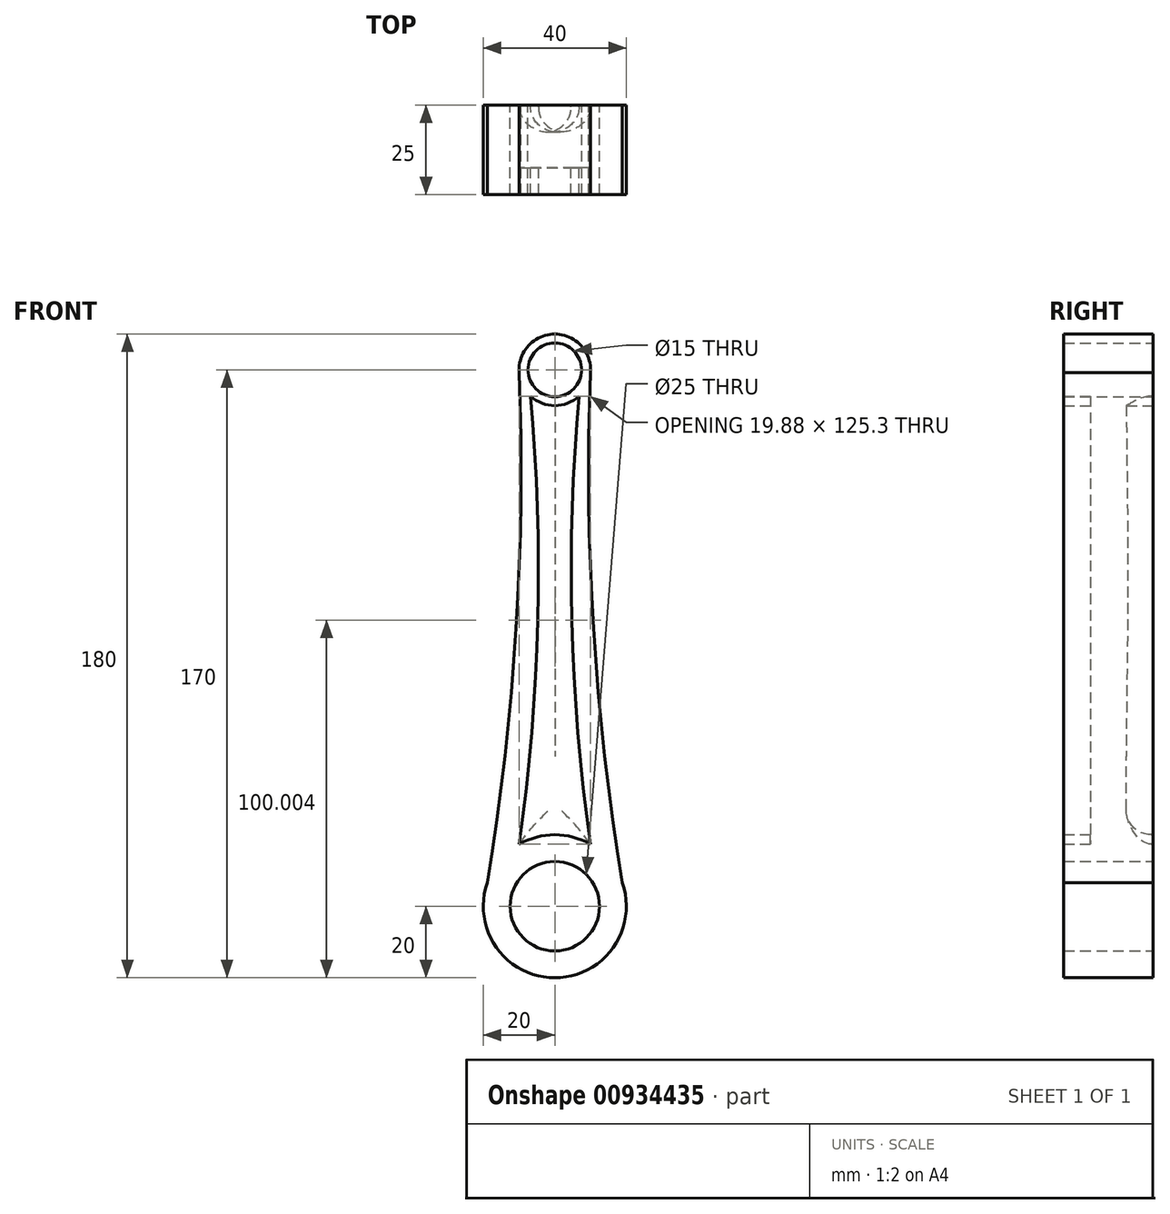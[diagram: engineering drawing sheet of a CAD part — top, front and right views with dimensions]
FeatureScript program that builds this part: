
annotation { "Feature Type Name" : "Feature", "Feature Type Description" : "" }
export const myFeature = defineFeature(function(context is Context, id is Id, definition is map)
    precondition{}
    {
        {
            var Q0;
            Q0=qCreatedBy(makeId("Front.planeOp"),FACE);
            var sketch = newSketch(context, id + "F0", { "sketchPlane" : qUnion([Q0])});
            skArc(sketch, "E0", {"start": v(-18.88, 6.6) * mm, "mid": v(15.38, -12.79) * mm, "end": v(-9.94, 17.36) * mm});
            skCircle(sketch, "E1", {"center": v(0, 150) * mm, "radius": 10 * mm});
            skCircle(sketch, "E2", {"center": v(0, 0) * mm, "radius": 12.5 * mm});
            skCircle(sketch, "E3", {"center": v(0, 150) * mm, "radius": 7.5 * mm});
            skLineSegment(sketch, "E4", {"start": v(0, 150) * mm, "end": v(-7.5, 150) * mm});
            skLineSegment(sketch, "E5", {"start": v(0, 0) * mm, "end": v(-20, 0) * mm});
            skArc(sketch, "E6", {"start": v(-20, 0) * mm, "mid": v(-11, 74.73) * mm, "end": v(-10, 150) * mm});
            skArc(sketch, "E7", {"start": v(-9.94, 17.36) * mm, "mid": v(-4.74, 79.91) * mm, "end": v(-6.78, 142.65) * mm});
            skArc(sketch, "E8.MirrorCS", {"start": v(9.94, 17.36) * mm, "mid": v(4.74, 79.91) * mm, "end": v(6.78, 142.65) * mm});
            skArc(sketch, "E9.MirrorCS", {"start": v(20, 0) * mm, "mid": v(11, 74.73) * mm, "end": v(10, 150) * mm});
            skCircle(sketch, "E10", {"center": v(0, 0) * mm, "radius": 20 * mm});
            skPoint(sketch, "E11.orphan", {"position": v(12.3, 2.24) * mm});
            skPoint(sketch, "E12.orphan", {"position": v(-12.3, 2.24) * mm});
            skArc(sketch, "E13.trimOffspring", {"start": v(-7.34, 148.47) * mm, "mid": v(-7.42, 149.24) * mm, "end": v(-7.5, 150) * mm});
            skArc(sketch, "E14.trimOffspring", {"start": v(7.34, 148.47) * mm, "mid": v(7.42, 149.24) * mm, "end": v(7.5, 150) * mm});
            skSolve(sketch);
        }
        {
            var Q0;
            Q0 = qSketchRegion(id + "F0", true);
            extrude(context, id + "F1", {"entities" : qUnion([Q0]), "endBound" : BoundingType.SYMMETRIC, "depth" : 25 * mm, "offsetDistance" : 25 * mm});
        }
        {
            var Q0;
            {var subQ0=sQuery(id+"F0.wireOp",EDGE,"E7");Q0=makeQuery(id+"F0.imprint","IMPRINT",FACE,{"disambiguationData":[TD([[makeQuery(id+"F0.imprint","IMPRINT",EDGE,{"derivedFrom":subQ0}),-1.0]])]});}
            extrude(context, id + "F2", {"entities" : qUnion([Q0]), "operationType" : NewBodyOperationType.ADD, "endBound" : BoundingType.SYMMETRIC, "depth" : 10 * mm, "offsetDistance" : 25 * mm});
        }
        {
            var Q0;
            Q0=makeQuery(id+"F2.opExtrude","CAP_EDGE",EDGE,{"disambiguationData":[OSD([sQuery(id+"F0.wireOp",EDGE,"E7")])],"isStart":false});
            var Q1;
            Q1=makeQuery(id+"F2.opExtrude","CAP_EDGE",EDGE,{"disambiguationData":[OSD([sQuery(id+"F0.wireOp",EDGE,"E8.MirrorCS")])],"isStart":false});
            var Q2;
            Q2=makeQuery(id+"F2.opExtrude","CAP_EDGE",EDGE,{"disambiguationData":[OSD([sQuery(id+"F0.wireOp",EDGE,"E10")])],"isStart":false});
            var Q3;
            Q3=makeQuery(id+"F2.opExtrude","CAP_EDGE",EDGE,{"disambiguationData":[OSD([sQuery(id+"F0.wireOp",EDGE,"E1")])],"isStart":false});
            var Q4;
            Q4=makeQuery(id+"F2.opExtrude","CAP_FACE",FACE,{"disambiguationData":[OSD([sQuery(id+"F0.wireOp",EDGE,"E1"),sQuery(id+"F0.wireOp",EDGE,"E7"),sQuery(id+"F0.wireOp",EDGE,"E8.MirrorCS"),sQuery(id+"F0.wireOp",EDGE,"E10")])],"isStart":true});
            fillet(context, id + "F3", {"entities" : qUnion([Q0, Q1, Q2, Q3, Q4]), "radius" : 7 * mm, "tangentPropagation" : true, "allowEdgeOverflow" : false});
        }
    });
